# Revit family: Domotics-DomesticRanges-GEWISS-SYSTEM_DATA-PHONE_SOCKET_ENG
name_source: partatom
category: Apparecchi elettrici
revit_build: Autodesk Revit 2016 (Build: 20161004_0715(x64)
units: mm (PartAtom-declared; Revit-internal decimal feet)

## family parameters
Condiviso = Sì
Host = Superficie
Mantenere orientamento annotazione = Sì
Numero OmniClass = 23.80.50.11.14
Punto di calcolo locali = Sì
Quota connettore circolare = Usa diametro
Taglio con vuoti quando caricato = Sì
Tipo di parte = Normale
Titolo OmniClass = Switches

## types (2) — shared parameters
Carico apparente = 0 VA
Catalogue = DOMOTICS
Catalogue Range = SYSTEM - DOMESTIC RANGE
Connection = Screw-on terminals
Description. = Telephone socket-outlet
Description: = British 6 contacts
Electrocod = 3721
Finitura pulsante = GEWISS ACCIAIO NERO
IDF = 0e5d4f40-860d-484c-97f0-836a3f57170f
IDT = 7866d6bf-aafb-40d5-8ada-9406e3f3ec0e
Immagine tipo = GW21272.jpg
Larghezza pulsante = 23 mm  [stored 0.0754593 ft]
N. poli = 1
No. SYSTEM modules = 1
Produttore = GEWISS S.p.A.
Prospetto di default = 1219 mm
SEO = Connector
Standard: = UK
Technical sheet = https://www.gewiss.com
Tipo_ = SYSTEM PRESE TEL ENG_BASE : GW21272 Presa telefonica Inglese 1M singola nero
URL = https://www.gewiss.com
Version file RFA = 19.4
Volt = 230 V

## per-type parameters (varying)
| type | Colour | Descrizione | EAN code | Modello |
| GW20272 - SINGLE 1M BRITISH PHONE SOCKET SY/WT | White | SINGLE 1M BRITISH PHONE SOCKET SY/WT | 8011564123847 | GW20272 |
| GW21272 - SINGLE 1M BRITISH PHONE SOCKET SY/BK | Black | SINGLE 1M BRITISH PHONE SOCKET SY/BK | 8011564128835 | GW21272 |

note: [stored X ft] marks values corroborated as IEEE doubles in the binary element streams (Revit-internal decimal feet)
